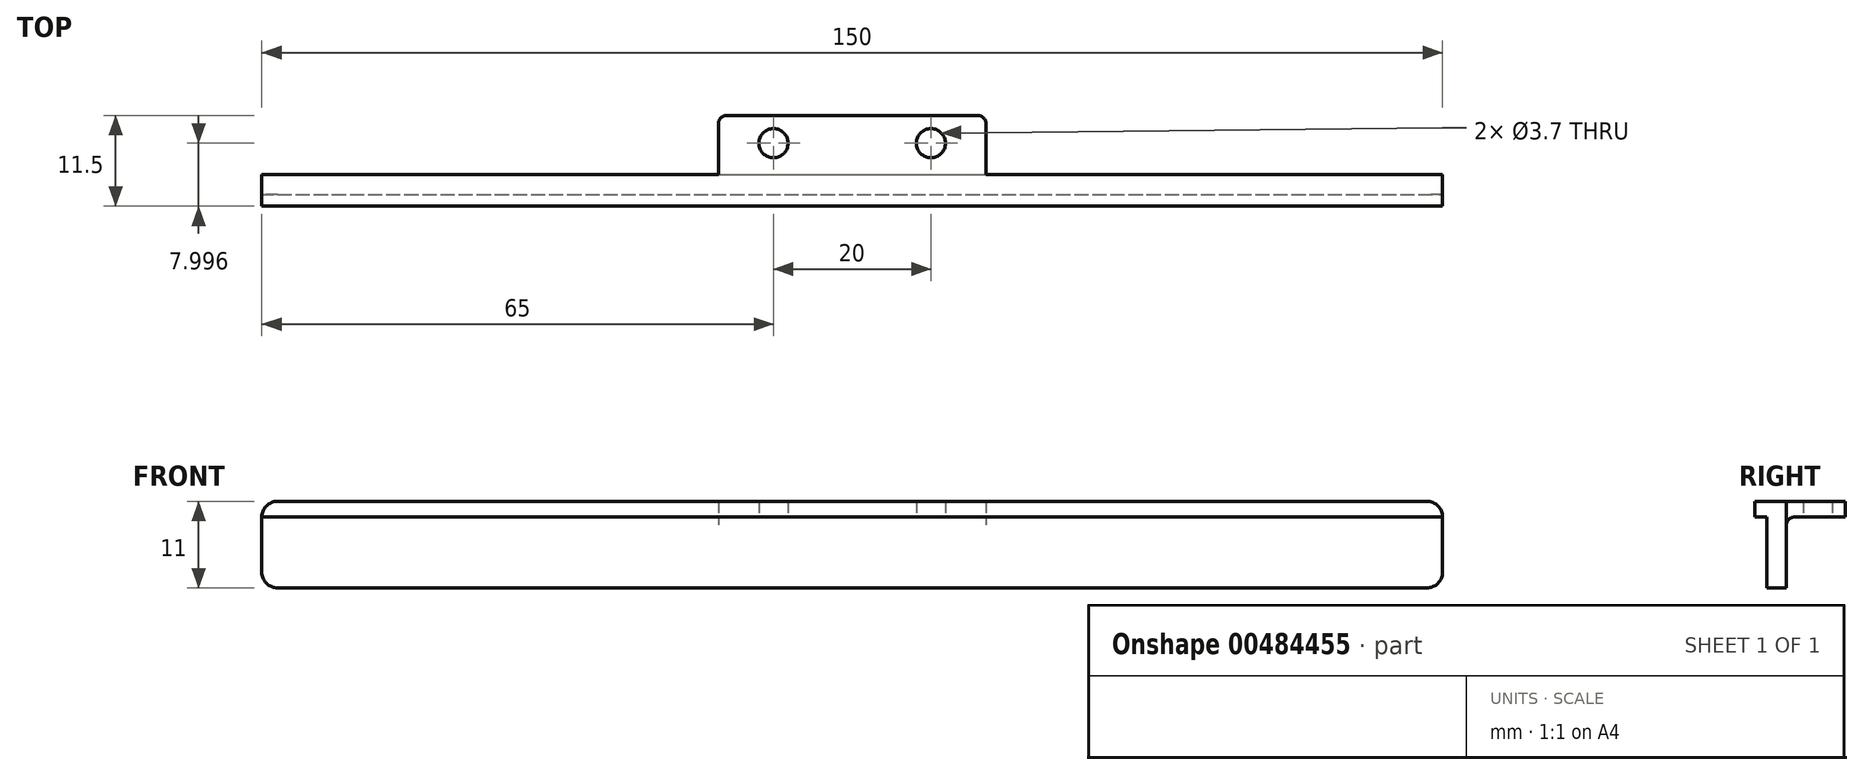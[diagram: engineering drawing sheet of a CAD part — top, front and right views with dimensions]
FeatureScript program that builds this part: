
annotation { "Feature Type Name" : "Feature", "Feature Type Description" : "" }
export const myFeature = defineFeature(function(context is Context, id is Id, definition is map)
    precondition{}
    {
        {
            var Q0;
            Q0=qCreatedBy(makeId("Top.planeOp"),FACE);
            var sketch = newSketch(context, id + "F0", { "sketchPlane" : qUnion([Q0])});
            skLineSegment(sketch, "E0.bottom", {"start": v(-20.24, 0.47) * mm, "end": v(13.76, 0.47) * mm});
            skLineSegment(sketch, "E0.top", {"start": v(-20.24, -9.53) * mm, "end": v(13.76, -9.53) * mm});
            skLineSegment(sketch, "E0.left", {"start": v(-20.24, 0.47) * mm, "end": v(-20.24, -9.53) * mm});
            skLineSegment(sketch, "E0.right", {"start": v(13.76, 0.47) * mm, "end": v(13.76, -9.53) * mm});
            skSolve(sketch);
        }
        {
            var Q0;
            Q0 = qSketchRegion(id + "F0", true);
            extrude(context, id + "F1", {"entities" : qUnion([Q0]), "depth" : 11 * mm});
        }
        {
            var Q0;
            Q0=makeQuery(id+"F1.opExtrude","SWEPT_FACE",FACE,{"disambiguationData":[OSD([sQuery(id+"F0.wireOp",EDGE,"E0.left")])]});
            var sketch = newSketch(context, id + "F2", { "sketchPlane" : qUnion([Q0])});
            skLineSegment(sketch, "E1.bottom", {"start": v(9.53, 11) * mm, "end": v(7.03, 11) * mm});
            skLineSegment(sketch, "E1.top", {"start": v(9.53, 0) * mm, "end": v(7.03, 0) * mm});
            skLineSegment(sketch, "E1.left", {"start": v(9.53, 11) * mm, "end": v(9.53, 0) * mm});
            skLineSegment(sketch, "E1.right", {"start": v(7.03, 11) * mm, "end": v(7.03, 0) * mm});
            skSolve(sketch);
        }
        {
            var Q0;
            Q0 = qSketchRegion(id + "F2", true);
            extrude(context, id + "F3", {"entities" : qUnion([Q0]), "operationType" : NewBodyOperationType.ADD, "depth" : 58 * mm});
        }
        {
            var Q0;
            Q0=makeQuery(id+"F1.opExtrude","SWEPT_FACE",FACE,{"disambiguationData":[OSD([sQuery(id+"F0.wireOp",EDGE,"E0.right")])]});
            var sketch = newSketch(context, id + "F4", { "sketchPlane" : qUnion([Q0])});
            skLineSegment(sketch, "E2.bottom", {"start": v(-9.53, 11) * mm, "end": v(-7.03, 11) * mm});
            skLineSegment(sketch, "E2.top", {"start": v(-9.53, 0) * mm, "end": v(-7.03, 0) * mm});
            skLineSegment(sketch, "E2.left", {"start": v(-9.53, 11) * mm, "end": v(-9.53, 0) * mm});
            skLineSegment(sketch, "E2.right", {"start": v(-7.03, 11) * mm, "end": v(-7.03, 0) * mm});
            skSolve(sketch);
        }
        {
            var Q0;
            Q0 = qSketchRegion(id + "F4", true);
            extrude(context, id + "F5", {"entities" : qUnion([Q0]), "operationType" : NewBodyOperationType.ADD, "depth" : 58 * mm});
        }
        {
            var Q0;
            Q0=makeQuery(id+"F1.opExtrude","SWEPT_FACE",FACE,{"disambiguationData":[OSD([sQuery(id+"F0.wireOp",EDGE,"E0.right")])]});
            var sketch = newSketch(context, id + "F6", { "sketchPlane" : qUnion([Q0])});
            skLineSegment(sketch, "E3.bottom", {"start": v(0.47, 0) * mm, "end": v(-7.03, 0) * mm});
            skLineSegment(sketch, "E3.top", {"start": v(0.47, 9) * mm, "end": v(-7.03, 9) * mm});
            skLineSegment(sketch, "E3.left", {"start": v(0.47, 0) * mm, "end": v(0.47, 9) * mm});
            skLineSegment(sketch, "E3.right", {"start": v(-7.03, 0) * mm, "end": v(-7.03, 9) * mm});
            skSolve(sketch);
        }
        {
            var Q0;
            Q0 = qSketchRegion(id + "F6", true);
            extrude(context, id + "F7", {"entities" : qUnion([Q0]), "operationType" : NewBodyOperationType.REMOVE, "endBound" : BoundingType.THROUGH_ALL, "oppositeDirection" : true, "depth" : 25 * mm});
        }
        {
            var Q0;
            Q0=makeQuery(id+"F7.boolean.opBoolean","COPY",FACE,{"derivedFrom":makeQuery(id+"F7.opExtrude","SWEPT_FACE",FACE,{"disambiguationData":[OSD([sQuery(id+"F6.wireOp",EDGE,"E3.top")])]})});
            var sketch = newSketch(context, id + "F8", { "sketchPlane" : qUnion([Q0])});
            skCircle(sketch, "E4", {"center": v(-13.24, 3.03) * mm, "radius": 1.85 * mm});
            skCircle(sketch, "E5", {"center": v(6.76, 3.03) * mm, "radius": 1.85 * mm});
            skSolve(sketch);
        }
        {
            var Q0;
            Q0 = qSketchRegion(id + "F8", true);
            extrude(context, id + "F9", {"entities" : qUnion([Q0]), "operationType" : NewBodyOperationType.REMOVE, "endBound" : BoundingType.THROUGH_ALL, "oppositeDirection" : true, "depth" : 25 * mm});
        }
        {
            var Q0;
            Q0=makeQuery(id+"F7.boolean.opBoolean","COPY",EDGE,{"derivedFrom":makeQuery(id+"F7.opExtrude","SWEPT_EDGE",EDGE,{"disambiguationData":[OSD([sQuery(id+"F4.wireOp",EDGE,"E2.right"),sQuery(id+"F6.wireOp",EDGE,"E3.top"),sQuery(id+"F6.wireOp",EDGE,"E3.right")])]})});
            var Q1;
            Q1=makeQuery(id+"F3.opExtrude","CAP_EDGE",EDGE,{"disambiguationData":[OSD([sQuery(id+"F2.wireOp",EDGE,"E1.right")])],"isStart":true});
            var Q2;
            Q2=makeQuery(id+"F5.opExtrude","CAP_EDGE",EDGE,{"disambiguationData":[OSD([sQuery(id+"F4.wireOp",EDGE,"E2.right")])],"isStart":true});
            var Q3;
            Q3=makeQuery(id+"F1.opExtrude","SWEPT_EDGE",EDGE,{"disambiguationData":[OSD([sQuery(id+"F0.wireOp",EDGE,"E0.bottom"),sQuery(id+"F0.wireOp",EDGE,"E0.left")])]});
            var Q4;
            Q4=makeQuery(id+"F1.opExtrude","SWEPT_EDGE",EDGE,{"disambiguationData":[OSD([sQuery(id+"F0.wireOp",EDGE,"E0.bottom"),sQuery(id+"F0.wireOp",EDGE,"E0.right")])]});
            fillet(context, id + "F10", {"entities" : qUnion([Q0, Q1, Q2, Q3, Q4]), "radius" : 1 * mm, "tangentPropagation" : true, "allowEdgeOverflow" : false});
        }
        {
            var Q0;
            Q0=makeQuery(id+"F5.boolean.opBoolean","MERGE",FACE,{"derivedFrom":[makeQuery(id+"F3.boolean.opBoolean","MERGE",FACE,{"derivedFrom":[makeQuery(id+"F1.opExtrude","SWEPT_FACE",FACE,{"disambiguationData":[OSD([sQuery(id+"F0.wireOp",EDGE,"E0.top")])]}),makeQuery(id+"F3.opExtrude","SWEPT_FACE",FACE,{"disambiguationData":[OSD([sQuery(id+"F2.wireOp",EDGE,"E1.left")])]})]}),makeQuery(id+"F5.opExtrude","SWEPT_FACE",FACE,{"disambiguationData":[OSD([sQuery(id+"F4.wireOp",EDGE,"E2.left")])]})]});
            var sketch = newSketch(context, id + "F11", { "sketchPlane" : qUnion([Q0])});
            skLineSegment(sketch, "E6.bottom", {"start": v(-78.24, 11) * mm, "end": v(71.76, 11) * mm});
            skLineSegment(sketch, "E6.top", {"start": v(-78.24, 9) * mm, "end": v(71.76, 9) * mm});
            skLineSegment(sketch, "E6.left", {"start": v(-78.24, 11) * mm, "end": v(-78.24, 9) * mm});
            skLineSegment(sketch, "E6.right", {"start": v(71.76, 11) * mm, "end": v(71.76, 9) * mm});
            skSolve(sketch);
        }
        {
            var Q0;
            Q0 = qSketchRegion(id + "F11", true);
            extrude(context, id + "F12", {"entities" : qUnion([Q0]), "operationType" : NewBodyOperationType.ADD, "depth" : 1.5 * mm});
        }
        {
            var Q0;
            Q0=makeQuery(id+"F12.boolean.opBoolean","MERGE",EDGE,{"derivedFrom":[makeQuery(id+"F3.opExtrude","CAP_EDGE",EDGE,{"disambiguationData":[OSD([sQuery(id+"F2.wireOp",EDGE,"E1.bottom")])],"isStart":false}),makeQuery(id+"F12.opExtrude","SWEPT_EDGE",EDGE,{"disambiguationData":[OSD([sQuery(id+"F11.wireOp",EDGE,"E6.bottom"),sQuery(id+"F11.wireOp",EDGE,"E6.left")])]})]});
            var Q1;
            Q1=makeQuery(id+"F3.opExtrude","CAP_EDGE",EDGE,{"disambiguationData":[OSD([sQuery(id+"F2.wireOp",EDGE,"E1.top")])],"isStart":false});
            var Q2;
            Q2=makeQuery(id+"F12.boolean.opBoolean","MERGE",EDGE,{"derivedFrom":[makeQuery(id+"F5.opExtrude","CAP_EDGE",EDGE,{"disambiguationData":[OSD([sQuery(id+"F4.wireOp",EDGE,"E2.bottom")])],"isStart":false}),makeQuery(id+"F12.opExtrude","SWEPT_EDGE",EDGE,{"disambiguationData":[OSD([sQuery(id+"F11.wireOp",EDGE,"E6.bottom"),sQuery(id+"F11.wireOp",EDGE,"E6.right")])]})]});
            var Q3;
            Q3=makeQuery(id+"F5.opExtrude","CAP_EDGE",EDGE,{"disambiguationData":[OSD([sQuery(id+"F4.wireOp",EDGE,"E2.top")])],"isStart":false});
            fillet(context, id + "F13", {"entities" : qUnion([Q0, Q1, Q2, Q3]), "radius" : 2 * mm, "tangentPropagation" : true, "allowEdgeOverflow" : false});
        }
    });
